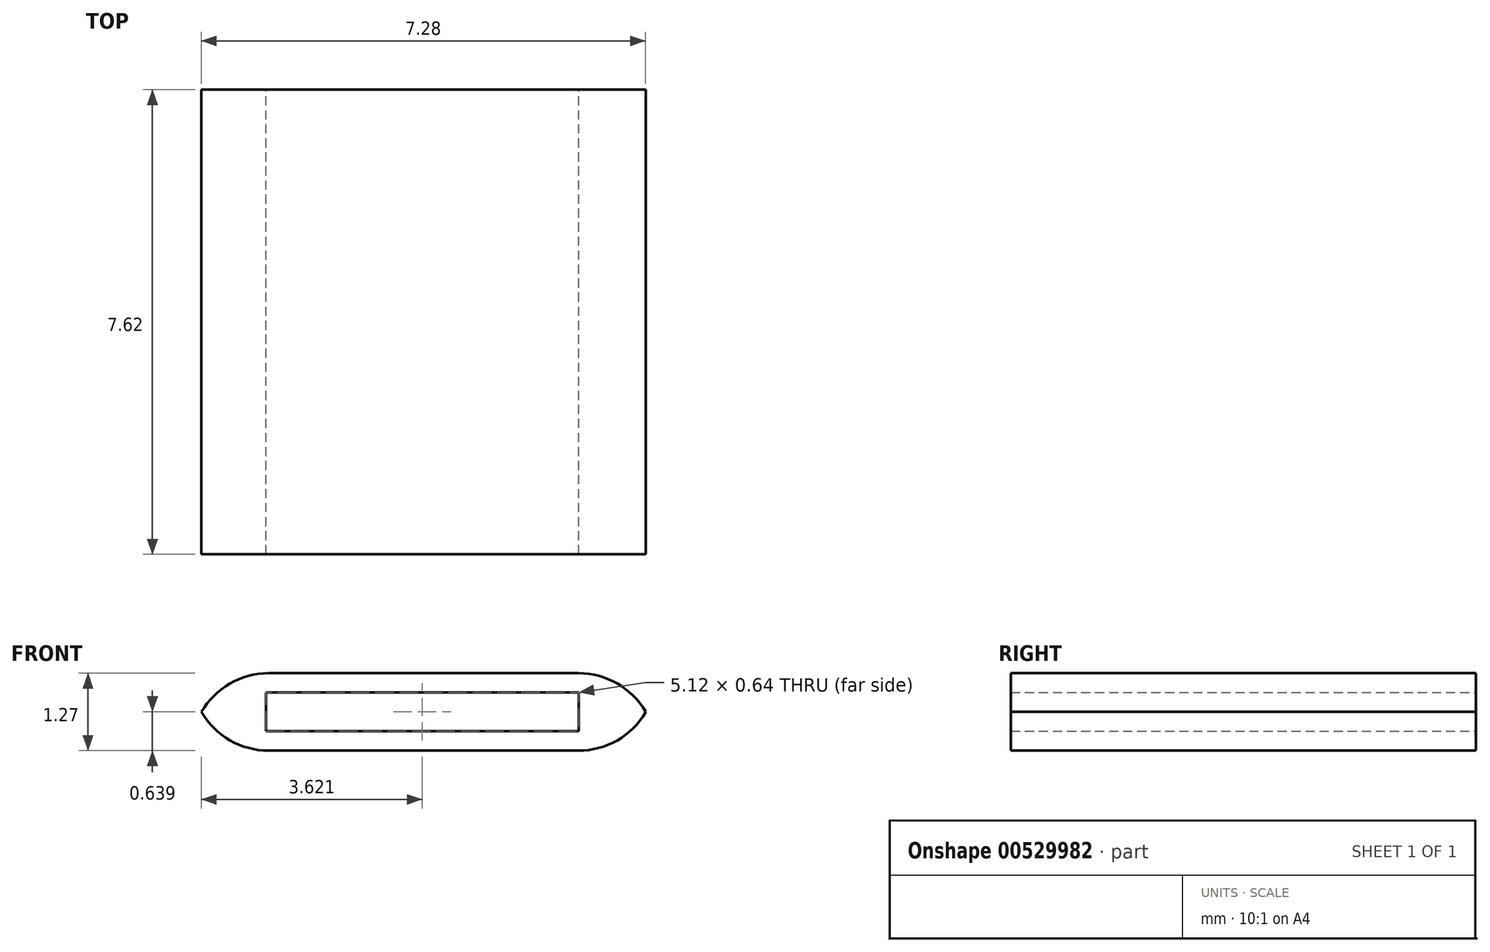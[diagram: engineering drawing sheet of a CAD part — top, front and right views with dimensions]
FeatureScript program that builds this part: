
annotation { "Feature Type Name" : "Feature", "Feature Type Description" : "" }
export const myFeature = defineFeature(function(context is Context, id is Id, definition is map)
    precondition{}
    {
        {
            var Q0;
            Q0=qCreatedBy(makeId("Top.planeOp"),FACE);
            var sketch = newSketch(context, id + "F0", { "sketchPlane" : qUnion([Q0])});
            skLineSegment(sketch, "E0.bottom", {"start": v(-38.69, 36.98) * mm, "end": v(-31.07, 36.98) * mm});
            skLineSegment(sketch, "E0.top", {"start": v(-38.69, 29.36) * mm, "end": v(-31.07, 29.36) * mm});
            skLineSegment(sketch, "E0.left", {"start": v(-38.69, 36.98) * mm, "end": v(-38.69, 29.36) * mm});
            skLineSegment(sketch, "E0.right", {"start": v(-31.07, 36.98) * mm, "end": v(-31.07, 29.36) * mm});
            skSolve(sketch);
        }
        {
            var Q0;
            Q0=makeQuery(id+"F0.imprint","IMPRINT",FACE,{"disambiguationData":[TD([[makeQuery(id+"F0.imprint","IMPRINT",EDGE,{"derivedFrom":sQuery(id+"F0.wireOp",EDGE,"E0.bottom")}),-1.0]])]});
            extrude(context, id + "F1", {"entities" : qUnion([Q0]), "depth" : 1.27 * mm, "offsetDistance" : 25.4 * mm});
        }
        {
            var Q0;
            Q0=makeQuery(id+"F1.opExtrude","CAP_EDGE",EDGE,{"disambiguationData":[OSD([sQuery(id+"F0.wireOp",EDGE,"E0.left")])],"isStart":false});
            var Q1;
            Q1=makeQuery(id+"F1.opExtrude","CAP_EDGE",EDGE,{"disambiguationData":[OSD([sQuery(id+"F0.wireOp",EDGE,"E0.right")])],"isStart":false});
            var Q2;
            Q2=makeQuery(id+"F1.opExtrude","CAP_EDGE",EDGE,{"disambiguationData":[OSD([sQuery(id+"F0.wireOp",EDGE,"E0.left")])],"isStart":true});
            var Q3;
            Q3=makeQuery(id+"F1.opExtrude","CAP_EDGE",EDGE,{"disambiguationData":[OSD([sQuery(id+"F0.wireOp",EDGE,"E0.right")])],"isStart":true});
            fillet(context, id + "F2", {"entities" : qUnion([Q0, Q1, Q2, Q3]), "radius" : 1.27 * mm, "tangentPropagation" : true, "allowEdgeOverflow" : false});
        }
        {
            var Q0;
            Q0=makeQuery(id+"F1.opExtrude","SWEPT_FACE",FACE,{"disambiguationData":[OSD([sQuery(id+"F0.wireOp",EDGE,"E0.bottom")])]});
            var sketch = newSketch(context, id + "F3", { "sketchPlane" : qUnion([Q0])});
            skLineSegment(sketch, "E1.bottom", {"start": v(32.34, 0.96) * mm, "end": v(37.46, 0.96) * mm});
            skLineSegment(sketch, "E1.top", {"start": v(32.34, 0.32) * mm, "end": v(37.46, 0.32) * mm});
            skLineSegment(sketch, "E1.left", {"start": v(32.34, 0.96) * mm, "end": v(32.34, 0.32) * mm});
            skLineSegment(sketch, "E1.right", {"start": v(37.46, 0.96) * mm, "end": v(37.46, 0.32) * mm});
            skSolve(sketch);
        }
        {
            var Q0;
            Q0=makeQuery(id+"F3.imprint","IMPRINT",FACE,{"disambiguationData":[TD([[makeQuery(id+"F3.imprint","IMPRINT",EDGE,{"derivedFrom":sQuery(id+"F3.wireOp",EDGE,"E1.bottom")}),-1.0]])]});
            extrude(context, id + "F4", {"entities" : qUnion([Q0]), "operationType" : NewBodyOperationType.REMOVE, "oppositeDirection" : true, "depth" : 7.62 * mm, "offsetDistance" : 25.4 * mm});
        }
    });
